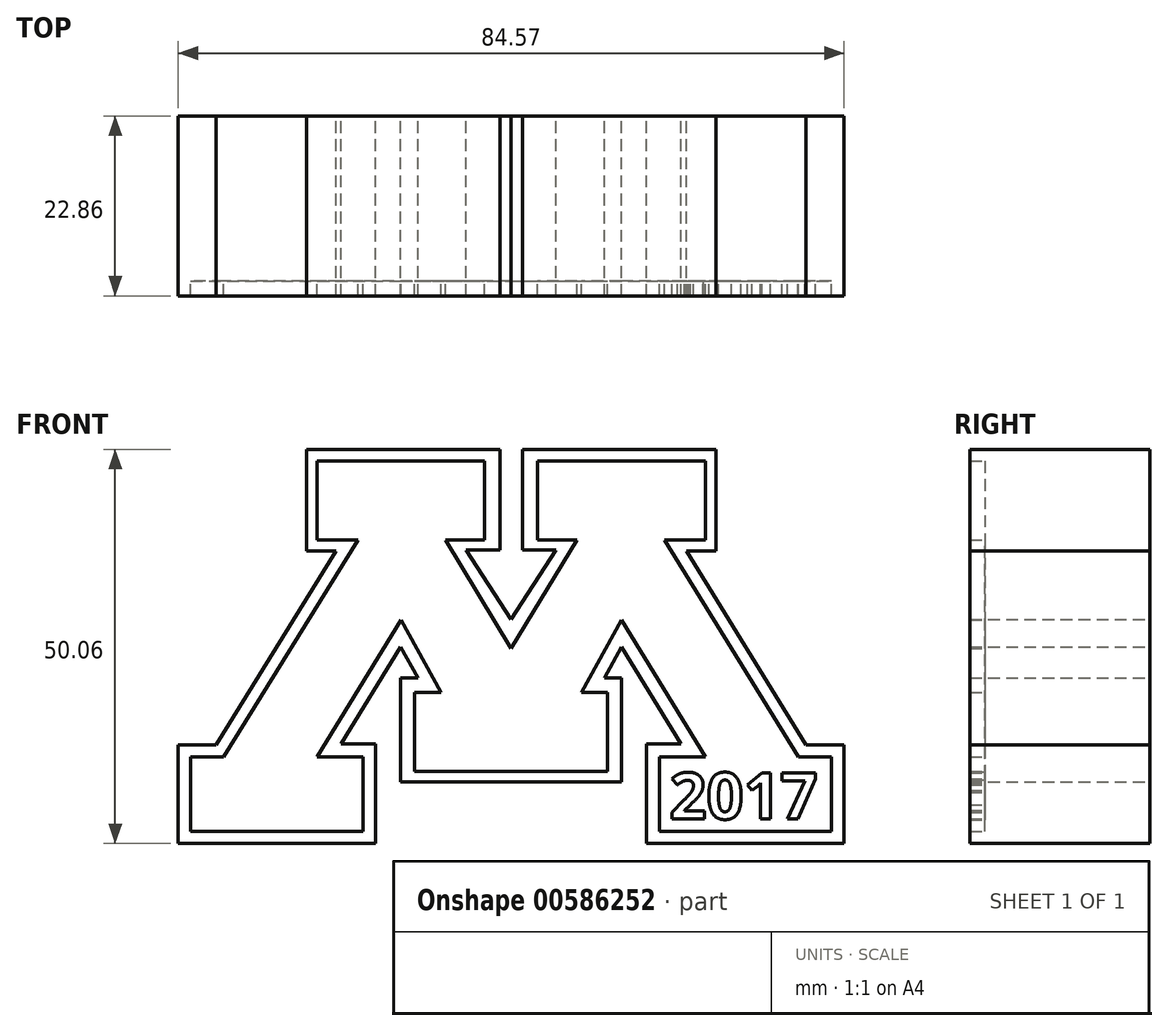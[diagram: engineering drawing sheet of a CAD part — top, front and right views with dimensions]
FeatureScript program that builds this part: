
annotation { "Feature Type Name" : "Feature", "Feature Type Description" : "" }
export const myFeature = defineFeature(function(context is Context, id is Id, definition is map)
    precondition{}
    {
        {
            var Q0;
            Q0=qCreatedBy(makeId("Front.planeOp"),FACE);
            var sketch = newSketch(context, id + "F0", { "sketchPlane" : qUnion([Q0])});
            skLineSegment(sketch, "E0", {"start": v(0, 39.68) * mm, "end": v(-3.81, 45.59) * mm});
            skLineSegment(sketch, "E1", {"start": v(-3.81, 45.59) * mm, "end": v(-0.96, 45.59) * mm});
            skLineSegment(sketch, "E2", {"start": v(-0.96, 45.59) * mm, "end": v(-0.96, 54.08) * mm});
            skLineSegment(sketch, "E3", {"start": v(-0.96, 54.08) * mm, "end": v(-17.34, 54.08) * mm});
            skLineSegment(sketch, "E4", {"start": v(-17.34, 54.08) * mm, "end": v(-17.34, 45.48) * mm});
            skLineSegment(sketch, "E5", {"start": v(-17.34, 45.48) * mm, "end": v(-14.83, 45.48) * mm});
            skLineSegment(sketch, "E6", {"start": v(-14.83, 45.48) * mm, "end": v(-24.98, 29.08) * mm});
            skLineSegment(sketch, "E7", {"start": v(-24.98, 29.08) * mm, "end": v(-28.19, 29.08) * mm});
            skLineSegment(sketch, "E8", {"start": v(-28.19, 29.08) * mm, "end": v(-28.19, 20.7) * mm});
            skLineSegment(sketch, "E9", {"start": v(-28.19, 20.7) * mm, "end": v(-11.46, 20.7) * mm});
            skLineSegment(sketch, "E10", {"start": v(-11.46, 20.7) * mm, "end": v(-11.46, 29.13) * mm});
            skLineSegment(sketch, "E11", {"start": v(-11.46, 29.13) * mm, "end": v(-14.4, 29.13) * mm});
            skLineSegment(sketch, "E12", {"start": v(-14.4, 29.13) * mm, "end": v(-9.35, 37.36) * mm});
            skLineSegment(sketch, "E13", {"start": v(-9.35, 37.36) * mm, "end": v(-7.9, 34.71) * mm});
            skLineSegment(sketch, "E14", {"start": v(-7.9, 34.71) * mm, "end": v(-9.35, 34.71) * mm});
            skLineSegment(sketch, "E15", {"start": v(-9.35, 34.71) * mm, "end": v(-9.35, 25.93) * mm});
            skLineSegment(sketch, "E16", {"start": v(-9.35, 25.93) * mm, "end": v(0, 25.93) * mm});
            skLineSegment(sketch, "E17", {"start": v(0, 25.93) * mm, "end": v(0, 39.68) * mm});
            skLineSegment(sketch, "E18", {"start": v(0, 37.23) * mm, "end": v(-5.56, 46.44) * mm});
            skLineSegment(sketch, "E19", {"start": v(-5.56, 46.44) * mm, "end": v(-2.24, 46.44) * mm});
            skLineSegment(sketch, "E20", {"start": v(-2.24, 46.44) * mm, "end": v(-2.24, 53.1) * mm});
            skLineSegment(sketch, "E21", {"start": v(-2.24, 53.1) * mm, "end": v(-16.44, 53.1) * mm});
            skLineSegment(sketch, "E22", {"start": v(-16.44, 53.1) * mm, "end": v(-16.44, 46.44) * mm});
            skLineSegment(sketch, "E23", {"start": v(-16.44, 46.44) * mm, "end": v(-12.98, 46.44) * mm});
            skLineSegment(sketch, "E24", {"start": v(-12.98, 46.44) * mm, "end": v(-24.34, 28.07) * mm});
            skLineSegment(sketch, "E25", {"start": v(-24.34, 28.07) * mm, "end": v(-27.13, 28.07) * mm});
            skLineSegment(sketch, "E26", {"start": v(-27.13, 28.07) * mm, "end": v(-27.13, 21.73) * mm});
            skLineSegment(sketch, "E27", {"start": v(-27.13, 21.73) * mm, "end": v(-12.55, 21.73) * mm});
            skLineSegment(sketch, "E28", {"start": v(-12.55, 21.73) * mm, "end": v(-12.55, 28.07) * mm});
            skLineSegment(sketch, "E29", {"start": v(-12.55, 28.07) * mm, "end": v(-16.44, 28.07) * mm});
            skLineSegment(sketch, "E30", {"start": v(-16.44, 28.07) * mm, "end": v(-9.34, 39.66) * mm});
            skLineSegment(sketch, "E31", {"start": v(-9.34, 39.66) * mm, "end": v(-5.95, 33.5) * mm});
            skLineSegment(sketch, "E32", {"start": v(-5.95, 33.5) * mm, "end": v(-8.18, 33.5) * mm});
            skLineSegment(sketch, "E33", {"start": v(-8.18, 33.5) * mm, "end": v(-8.18, 26.83) * mm});
            skLineSegment(sketch, "E34", {"start": v(-8.18, 26.83) * mm, "end": v(0, 26.83) * mm});
            skSolve(sketch);
        }
        {
            var Q0;
            {var subQ0=sQuery(id+"F0.wireOp",EDGE,"E18");Q0=makeQuery(id+"F0.imprint","IMPRINT",FACE,{"disambiguationData":[TD([[makeQuery(id+"F0.imprint","IMPRINT",EDGE,{"derivedFrom":subQ0}),1.0]])]});}
            extrude(context, id + "F1", {"entities" : qUnion([Q0]), "depth" : 13.97 * mm, "offsetDistance" : 25.4 * mm});
        }
        {
            var Q0;
            {var subQ2=sQuery(id+"F0.wireOp",EDGE,"E0");Q0=makeQuery(id+"F0.imprint","IMPRINT",FACE,{"disambiguationData":[TD([[makeQuery(id+"F0.imprint","IMPRINT",EDGE,{"derivedFrom":subQ2}),1.0]])]});}
            extrude(context, id + "F2", {"entities" : qUnion([Q0]), "operationType" : NewBodyOperationType.ADD, "depth" : 15.24 * mm, "offsetDistance" : 25.4 * mm});
        }
        {
            var Q0;
            Q0=makeQuery(id+"F1.opExtrude","SWEPT_BODY",BODY,{"disambiguationData":[OSD([sQuery(id+"F0.wireOp",EDGE,"E17"),sQuery(id+"F0.wireOp",EDGE,"E18"),sQuery(id+"F0.wireOp",EDGE,"E19"),sQuery(id+"F0.wireOp",EDGE,"E20"),sQuery(id+"F0.wireOp",EDGE,"E21"),sQuery(id+"F0.wireOp",EDGE,"E22"),sQuery(id+"F0.wireOp",EDGE,"E23"),sQuery(id+"F0.wireOp",EDGE,"E24"),sQuery(id+"F0.wireOp",EDGE,"E25"),sQuery(id+"F0.wireOp",EDGE,"E26"),sQuery(id+"F0.wireOp",EDGE,"E27"),sQuery(id+"F0.wireOp",EDGE,"E28"),sQuery(id+"F0.wireOp",EDGE,"E29"),sQuery(id+"F0.wireOp",EDGE,"E30"),sQuery(id+"F0.wireOp",EDGE,"E31"),sQuery(id+"F0.wireOp",EDGE,"E32"),sQuery(id+"F0.wireOp",EDGE,"E33"),sQuery(id+"F0.wireOp",EDGE,"E34")])]});
            var Q1;
            {var subQ0=sQuery(id+"F0.wireOp",EDGE,"E17");Q1=makeQuery(id+"F2.boolean.opBoolean","MERGE",FACE,{"derivedFrom":[makeQuery(id+"F1.opExtrude","SWEPT_FACE",FACE,{"disambiguationData":[OSD([subQ0])]}),makeQuery(id+"F2.opExtrude","SWEPT_FACE",FACE,{"disambiguationData":[OSD([subQ0]),TDD([makeQuery(id+"F0.imprint","IMPRINT",EDGE,{"disambiguationData":[TD([[makeQuery(id+"F0.imprint","INTERSECT",VERTEX,{"derivedFrom":[sQuery(id+"F0.wireOp",EDGE,"E16"),subQ0]}),-1.0]])],"derivedFrom":subQ0})])]}),makeQuery(id+"F2.opExtrude","SWEPT_FACE",FACE,{"disambiguationData":[OSD([subQ0]),TDD([makeQuery(id+"F0.imprint","IMPRINT",EDGE,{"disambiguationData":[TD([[makeQuery(id+"F0.imprint","INTERSECT",VERTEX,{"derivedFrom":[sQuery(id+"F0.wireOp",EDGE,"E0"),subQ0]}),1.0]])],"derivedFrom":subQ0})])]})]});}
            mirror(context, id + "F3", {"operationType" : NewBodyOperationType.ADD, "entities" : qUnion([Q0]), "mirrorPlane" : qUnion([Q1])});
        }
        {
            var Q0;
            Q0=qCreatedBy(makeId("Front.planeOp"),FACE);
            var sketch = newSketch(context, id + "F4", { "sketchPlane" : qUnion([Q0])});
            skText(sketch, "E35", { "text": "2017", "fontName": "OpenSans-Bold.ttf"});
            const initialGuessF4  = {"E35": [0.01341, 0.02278, 1, 0, 0.00395]};
            skSetInitialGuess(sketch, initialGuessF4);
            skSolve(sketch);
        }
        {
            var Q0;
            Q0 = qSketchRegion(id + "F4", true);
            extrude(context, id + "F5", {"entities" : qUnion([Q0]), "operationType" : NewBodyOperationType.ADD, "depth" : 15.24 * mm, "offsetDistance" : 25.4 * mm});
        }
        {
            var Q0;
            Q0=makeQuery(id+"F1.opExtrude","SWEPT_BODY",BODY,{"disambiguationData":[OSD([sQuery(id+"F0.wireOp",EDGE,"E17"),sQuery(id+"F0.wireOp",EDGE,"E18"),sQuery(id+"F0.wireOp",EDGE,"E19"),sQuery(id+"F0.wireOp",EDGE,"E20"),sQuery(id+"F0.wireOp",EDGE,"E21"),sQuery(id+"F0.wireOp",EDGE,"E22"),sQuery(id+"F0.wireOp",EDGE,"E23"),sQuery(id+"F0.wireOp",EDGE,"E24"),sQuery(id+"F0.wireOp",EDGE,"E25"),sQuery(id+"F0.wireOp",EDGE,"E26"),sQuery(id+"F0.wireOp",EDGE,"E27"),sQuery(id+"F0.wireOp",EDGE,"E28"),sQuery(id+"F0.wireOp",EDGE,"E29"),sQuery(id+"F0.wireOp",EDGE,"E30"),sQuery(id+"F0.wireOp",EDGE,"E31"),sQuery(id+"F0.wireOp",EDGE,"E32"),sQuery(id+"F0.wireOp",EDGE,"E33"),sQuery(id+"F0.wireOp",EDGE,"E34")])]});
            var Q1;
            Q1=makeQuery(id+"F3.opPattern","COPY",VERTEX,{"derivedFrom":makeQuery(id+"F2.opExtrude","CAP_VERTEX",VERTEX,{"disambiguationData":[OSD([sQuery(id+"F0.wireOp",EDGE,"E8"),sQuery(id+"F0.wireOp",EDGE,"E9")])],"isStart":true}),"instanceName":"1"});
            transform(context, id + "F6", {"entities" : qUnion([Q0]), "transformType" : TransformType.SCALE_UNIFORMLY, "scale" : 1.5, "scalePoint" : qUnion([Q1]), "makeCopy" : false});
        }
    });
